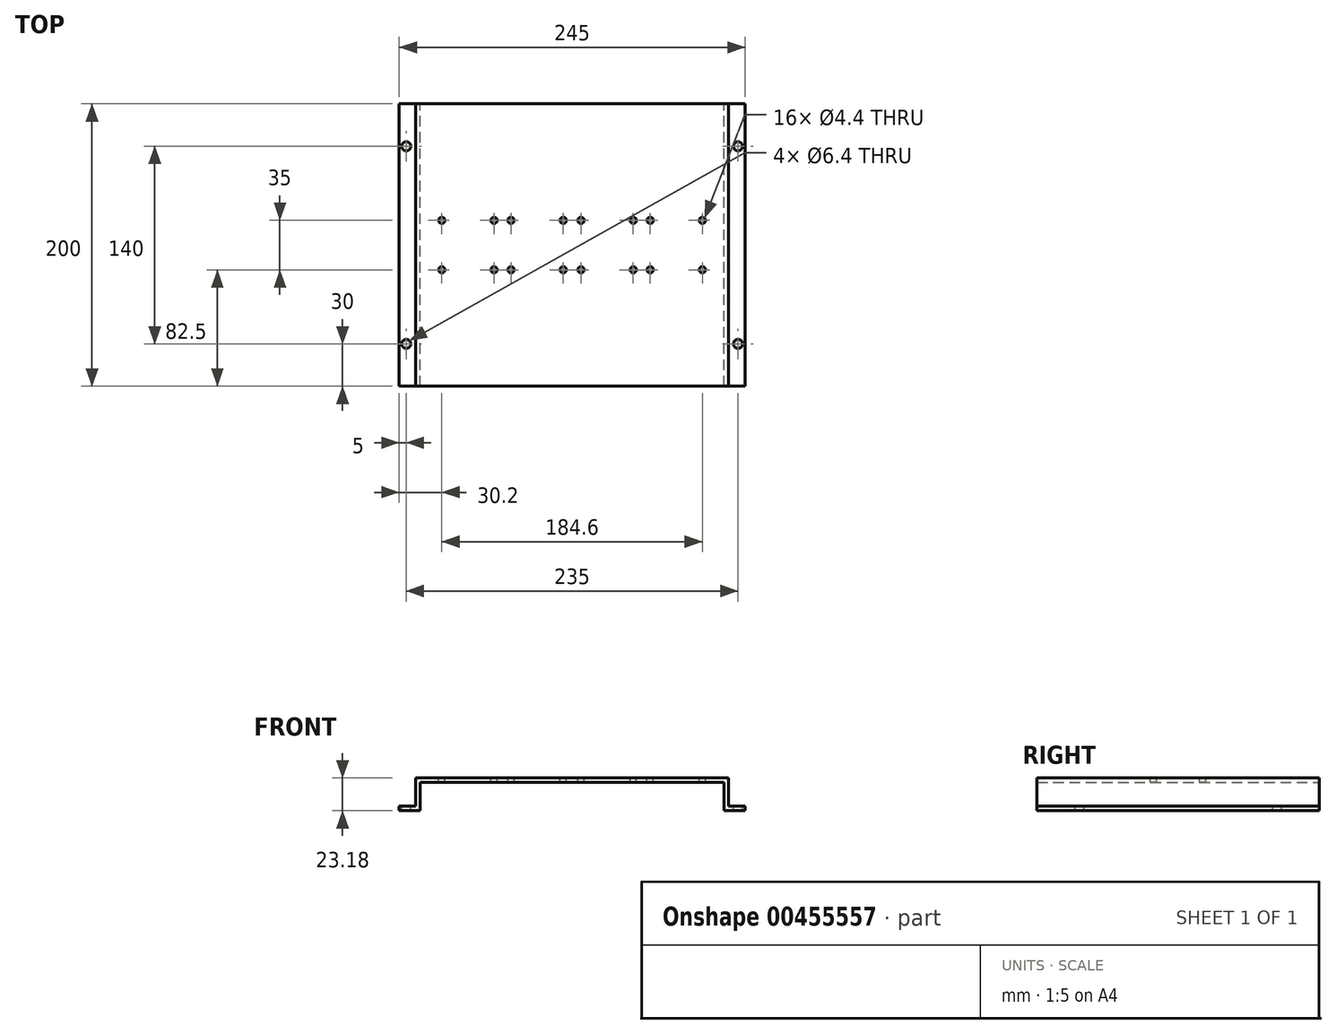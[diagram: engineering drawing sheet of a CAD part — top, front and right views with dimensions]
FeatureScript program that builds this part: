
annotation { "Feature Type Name" : "Feature", "Feature Type Description" : "" }
export const myFeature = defineFeature(function(context is Context, id is Id, definition is map)
    precondition{}
    {
        {
            var Q0;
            Q0=qCreatedBy(makeId("Front.planeOp"),FACE);
            var sketch = newSketch(context, id + "F0", { "sketchPlane" : qUnion([Q0])});
            skLineSegment(sketch, "E0.bottom", {"start": v(107.5, 10) * mm, "end": v(-107.5, 10) * mm});
            skLineSegment(sketch, "E0.top", {"start": v(122.5, -10) * mm, "end": v(107.5, -10) * mm});
            skLineSegment(sketch, "E0.left", {"start": v(122.5, -6.83) * mm, "end": v(122.5, -10) * mm});
            skLineSegment(sketch, "E0.right", {"start": v(-122.5, -6.83) * mm, "end": v(-122.5, -10) * mm});
            skPoint(sketch, "E0.middle", {"position": v(0, 0) * mm});
            skLineSegment(sketch, "E1.0", {"start": v(122.5, -6.83) * mm, "end": v(110.67, -6.83) * mm});
            skLineSegment(sketch, "E2.0", {"start": v(110.67, 13.17) * mm, "end": v(-110.67, 13.17) * mm});
            skLineSegment(sketch, "E3", {"start": v(-122.5, -10) * mm, "end": v(-107.5, -10) * mm});
            skLineSegment(sketch, "E4", {"start": v(-107.5, -10) * mm, "end": v(-107.5, 10) * mm});
            skLineSegment(sketch, "E5.0", {"start": v(-110.67, -6.83) * mm, "end": v(-110.67, 13.17) * mm});
            skPoint(sketch, "E6.orphan", {"position": v(-122.5, 10) * mm});
            skLineSegment(sketch, "E7.trimOffspring", {"start": v(-110.67, -6.83) * mm, "end": v(-122.5, -6.83) * mm});
            skPoint(sketch, "E8.MirrorP", {"position": v(122.5, 10) * mm});
            skLineSegment(sketch, "E9.MirrorCS", {"start": v(110.67, -6.83) * mm, "end": v(122.5, -6.83) * mm});
            skLineSegment(sketch, "E10.MirrorCS", {"start": v(110.67, -6.83) * mm, "end": v(110.67, 13.17) * mm});
            skLineSegment(sketch, "E11.MirrorCS", {"start": v(107.5, -10) * mm, "end": v(107.5, 10) * mm});
            skPoint(sketch, "E12.trimOffspring.end.orphan", {"position": v(-107.5, -6.83) * mm});
            skPoint(sketch, "E12.trimOffspring.start.orphan", {"position": v(107.5, -6.83) * mm});
            skLineSegment(sketch, "E13.trimOffspring", {"start": v(-107.5, -10) * mm, "end": v(-122.5, -10) * mm});
            skSolve(sketch);
        }
        {
            var Q0;
            Q0=makeQuery(id+"F0.imprint","IMPRINT",FACE,{"disambiguationData":[TD([[makeQuery(id+"F0.imprint","IMPRINT",EDGE,{"derivedFrom":sQuery(id+"F0.wireOp",EDGE,"E0.bottom")}),-1.0]])]});
            extrude(context, id + "F1", {"entities" : qUnion([Q0]), "endBound" : BoundingType.SYMMETRIC, "depth" : 200 * mm});
        }
        {
            var Q0;
            Q0=qCreatedBy(makeId("Top.planeOp"),FACE);
            var sketch = newSketch(context, id + "F2", { "sketchPlane" : qUnion([Q0])});
            skCircle(sketch, "E14", {"center": v(-117.5, -70) * mm, "radius": 3.2 * mm});
            skCircle(sketch, "E15", {"center": v(-92.3, -17.5) * mm, "radius": 2.2 * mm});
            skCircle(sketch, "E16", {"center": v(-55.3, -17.5) * mm, "radius": 2.2 * mm});
            skCircle(sketch, "E17", {"center": v(-43.3, -17.5) * mm, "radius": 2.2 * mm});
            skCircle(sketch, "E18", {"center": v(-6.3, -17.5) * mm, "radius": 2.2 * mm});
            skCircle(sketch, "E19.MirrorC", {"center": v(6.3, -17.5) * mm, "radius": 2.2 * mm});
            skCircle(sketch, "E20.MirrorC", {"center": v(43.3, -17.5) * mm, "radius": 2.2 * mm});
            skCircle(sketch, "E21.MirrorC", {"center": v(55.3, -17.5) * mm, "radius": 2.2 * mm});
            skCircle(sketch, "E22.MirrorC", {"center": v(92.3, -17.5) * mm, "radius": 2.2 * mm});
            skCircle(sketch, "E23.MirrorC", {"center": v(117.5, -70) * mm, "radius": 3.2 * mm});
            skCircle(sketch, "E24.MirrorC", {"center": v(-92.3, 17.5) * mm, "radius": 2.2 * mm});
            skCircle(sketch, "E25.MirrorC", {"center": v(43.3, 17.5) * mm, "radius": 2.2 * mm});
            skCircle(sketch, "E26.MirrorC", {"center": v(55.3, 17.5) * mm, "radius": 2.2 * mm});
            skCircle(sketch, "E27.MirrorC", {"center": v(6.3, 17.5) * mm, "radius": 2.2 * mm});
            skCircle(sketch, "E28.MirrorC", {"center": v(-6.3, 17.5) * mm, "radius": 2.2 * mm});
            skCircle(sketch, "E29.MirrorC", {"center": v(-43.3, 17.5) * mm, "radius": 2.2 * mm});
            skCircle(sketch, "E30.MirrorC", {"center": v(92.3, 17.5) * mm, "radius": 2.2 * mm});
            skCircle(sketch, "E31.MirrorC", {"center": v(-55.3, 17.5) * mm, "radius": 2.2 * mm});
            skCircle(sketch, "E32.MirrorC", {"center": v(-117.5, 70) * mm, "radius": 3.2 * mm});
            skCircle(sketch, "E33.MirrorC", {"center": v(117.5, 70) * mm, "radius": 3.2 * mm});
            skSolve(sketch);
        }
        {
            var Q0;
            Q0 = qSketchRegion(id + "F2", true);
            extrude(context, id + "F3", {"entities" : qUnion([Q0]), "operationType" : NewBodyOperationType.REMOVE, "endBound" : BoundingType.THROUGH_ALL, "oppositeDirection" : true, "depth" : 25 * mm, "hasSecondDirection" : true, "secondDirectionBound" : SecondDirectionBoundingType.THROUGH_ALL, "secondDirectionOppositeDirection" : false, "secondDirectionDepth" : 25 * mm});
        }
    });
